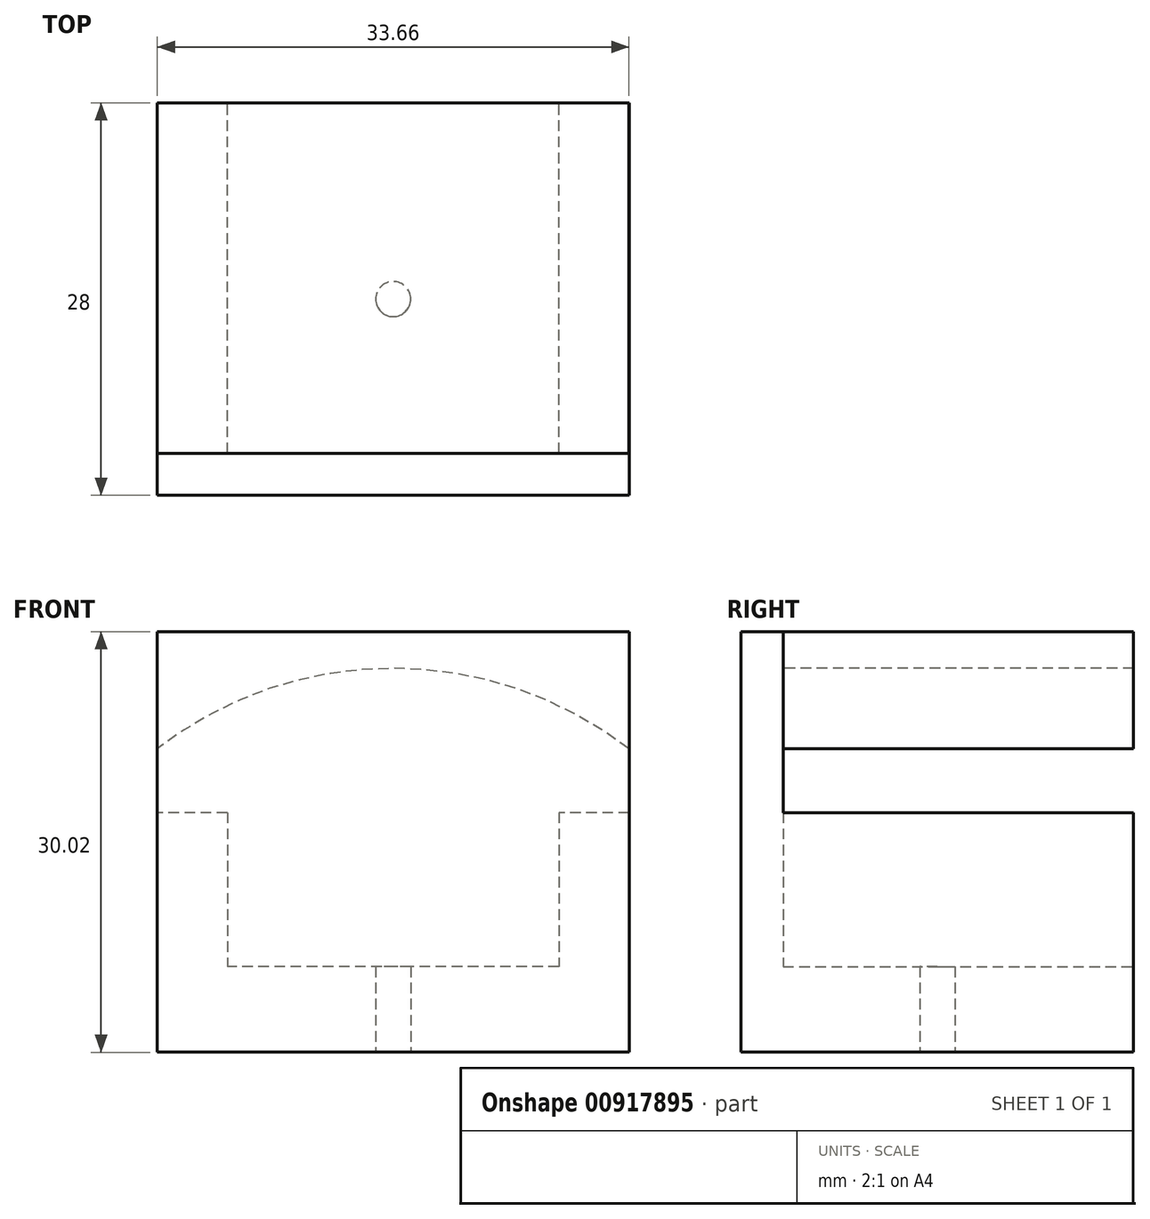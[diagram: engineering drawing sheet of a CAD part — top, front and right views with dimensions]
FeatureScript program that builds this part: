
annotation { "Feature Type Name" : "Feature", "Feature Type Description" : "" }
export const myFeature = defineFeature(function(context is Context, id is Id, definition is map)
    precondition{}
    {
        {
            var Q0;
            Q0=qCreatedBy(makeId("Front.planeOp"),FACE);
            var sketch = newSketch(context, id + "F0", { "sketchPlane" : qUnion([Q0])});
            skLineSegment(sketch, "E0.bottom", {"start": v(-12.4, 16.5) * mm, "end": v(21.24, 16.5) * mm});
            skLineSegment(sketch, "E0.top", {"start": v(-12.4, -13.6) * mm, "end": v(21.24, -13.6) * mm});
            skLineSegment(sketch, "E0.left", {"start": v(-12.4, 16.5) * mm, "end": v(-12.4, -13.6) * mm});
            skLineSegment(sketch, "E0.right", {"start": v(21.24, 16.5) * mm, "end": v(21.24, -13.6) * mm});
            skSolve(sketch);
        }
        {
            var Q0;
            Q0=makeQuery(id+"F0.imprint","IMPRINT",FACE,{"disambiguationData":[TD([[makeQuery(id+"F0.imprint","IMPRINT",EDGE,{"derivedFrom":sQuery(id+"F0.wireOp",EDGE,"E0.bottom")}),-1.0]])]});
            extrude(context, id + "F1", {"entities" : qUnion([Q0]), "depth" : 25 * mm, "offsetDistance" : 25 * mm});
        }
        {
            var Q0;
            Q0=makeQuery(id+"F1.opExtrude","CAP_FACE",FACE,{"disambiguationData":[OSD([sQuery(id+"F0.wireOp",EDGE,"E0.bottom"),sQuery(id+"F0.wireOp",EDGE,"E0.top"),sQuery(id+"F0.wireOp",EDGE,"E0.left"),sQuery(id+"F0.wireOp",EDGE,"E0.right")])],"isStart":false});
            var sketch = newSketch(context, id + "F2", { "sketchPlane" : qUnion([Q0])});
            skLineSegment(sketch, "E1", {"start": v(4.43, -13.6) * mm, "end": v(4.43, 16.5) * mm});
            skSolve(sketch);
        }
        {
            var Q0;
            Q0=sQuery(id+"F2.wireOp",VERTEX,"E1.start");
            var Q1;
            Q1=makeQuery(id+"F1.opExtrude","SWEPT_BODY",BODY,{"disambiguationData":[OSD([sQuery(id+"F0.wireOp",EDGE,"E0.bottom"),sQuery(id+"F0.wireOp",EDGE,"E0.top"),sQuery(id+"F0.wireOp",EDGE,"E0.left"),sQuery(id+"F0.wireOp",EDGE,"E0.right")])]});
            hole(context, id + "F3", {"style" : HoleStyle.SIMPLE, "endStyle" : HoleEndStyle.BLIND, "holeDiameter" : 55 * mm, "majorDiameter" : 5 * mm, "holeDepth" : 50 * mm, "isTappedThrough" : true, "tappedDepth" : 12 * mm, "tapClearance" : 3, "locations" : qUnion([Q0]), "scope" : qUnion([Q1])});
        }
        {
            var Q0;
            Q0=makeQuery(id+"F1.opExtrude","CAP_FACE",FACE,{"disambiguationData":[OSD([sQuery(id+"F0.wireOp",EDGE,"E0.bottom"),sQuery(id+"F0.wireOp",EDGE,"E0.top"),sQuery(id+"F0.wireOp",EDGE,"E0.left"),sQuery(id+"F0.wireOp",EDGE,"E0.right")])],"isStart":false});
            var sketch = newSketch(context, id + "F4", { "sketchPlane" : qUnion([Q0])});
            skLineSegment(sketch, "E2.bottom", {"start": v(-12.4, 16.5) * mm, "end": v(21.27, 16.5) * mm});
            skLineSegment(sketch, "E2.top", {"start": v(-12.4, -13.52) * mm, "end": v(21.27, -13.52) * mm});
            skLineSegment(sketch, "E2.left", {"start": v(-12.4, 16.5) * mm, "end": v(-12.4, -13.52) * mm});
            skLineSegment(sketch, "E2.right", {"start": v(21.27, 16.5) * mm, "end": v(21.27, -13.52) * mm});
            skSolve(sketch);
        }
        {
            var Q0;
            Q0 = qSketchRegion(id + "F4", true);
            extrude(context, id + "F5", {"entities" : qUnion([Q0]), "depth" : 3 * mm, "offsetDistance" : 25 * mm});
        }
        {
            var Q0;
            Q0=makeQuery(id+"F5.opExtrude","CAP_FACE",FACE,{"disambiguationData":[OSD([sQuery(id+"F4.wireOp",EDGE,"E2.bottom"),sQuery(id+"F4.wireOp",EDGE,"E2.top"),sQuery(id+"F4.wireOp",EDGE,"E2.left"),sQuery(id+"F4.wireOp",EDGE,"E2.right")])],"isStart":true});
            var sketch = newSketch(context, id + "F6", { "sketchPlane" : qUnion([Q0])});
            skLineSegment(sketch, "E3.bottom", {"start": v(-21.27, -13.52) * mm, "end": v(12.4, -13.52) * mm});
            skLineSegment(sketch, "E3.top", {"start": v(-21.27, -7.4) * mm, "end": v(12.4, -7.4) * mm});
            skLineSegment(sketch, "E3.left", {"start": v(-21.27, -13.52) * mm, "end": v(-21.27, -7.4) * mm});
            skLineSegment(sketch, "E3.right", {"start": v(12.4, -13.52) * mm, "end": v(12.4, -7.4) * mm});
            skSolve(sketch);
        }
        {
            var Q0;
            Q0=makeQuery(id+"F6.imprint","IMPRINT",FACE,{"disambiguationData":[TD([[makeQuery(id+"F6.imprint","IMPRINT",EDGE,{"derivedFrom":sQuery(id+"F6.wireOp",EDGE,"E3.bottom")}),-1.0]])]});
            extrude(context, id + "F7", {"entities" : qUnion([Q0]), "operationType" : NewBodyOperationType.ADD, "depth" : 25 * mm, "offsetDistance" : 25 * mm});
        }
        {
            var Q0;
            Q0=makeQuery(id+"F7.boolean.opBoolean","MERGE",FACE,{"derivedFrom":[makeQuery(id+"F5.opExtrude","SWEPT_FACE",FACE,{"disambiguationData":[OSD([sQuery(id+"F4.wireOp",EDGE,"E2.top")])]}),makeQuery(id+"F7.opExtrude","SWEPT_FACE",FACE,{"disambiguationData":[OSD([sQuery(id+"F6.wireOp",EDGE,"E3.bottom")])]})]});
            var sketch = newSketch(context, id + "F8", { "sketchPlane" : qUnion([Q0])});
            skLineSegment(sketch, "E4", {"start": v(-12.4, 28) * mm, "end": v(21.27, 0) * mm});
            skLineSegment(sketch, "E5", {"start": v(21.27, 0) * mm, "end": v(21.27, 28) * mm});
            skLineSegment(sketch, "E6", {"start": v(21.27, 28) * mm, "end": v(-12.4, 0) * mm});
            skLineSegment(sketch, "E7", {"start": v(-12.4, 0) * mm, "end": v(4.44, 14) * mm});
            skLineSegment(sketch, "E8", {"start": v(4.44, 14) * mm, "end": v(4.44, 0.89) * mm});
            skLineSegment(sketch, "E9", {"start": v(4.44, 0.89) * mm, "end": v(4.44, 28) * mm});
            skSolve(sketch);
        }
        {
            var Q0;
            Q0=sQuery(id+"F8.wireOp",VERTEX,"E7.end");
            var Q1;
            Q1=makeQuery(id+"F5.opExtrude","SWEPT_BODY",BODY,{"disambiguationData":[OSD([sQuery(id+"F4.wireOp",EDGE,"E2.bottom"),sQuery(id+"F4.wireOp",EDGE,"E2.top"),sQuery(id+"F4.wireOp",EDGE,"E2.left"),sQuery(id+"F4.wireOp",EDGE,"E2.right")])]});
            hole(context, id + "F9", {"style" : HoleStyle.SIMPLE, "endStyle" : HoleEndStyle.BLIND, "holeDiameter" : 2.5 * mm, "majorDiameter" : 5 * mm, "holeDepth" : 10 * mm, "isTappedThrough" : true, "tappedDepth" : 12 * mm, "tapClearance" : 3, "locations" : qUnion([Q0]), "scope" : qUnion([Q1])});
        }
        {
            var Q0;
            Q0=makeQuery(id+"F7.opExtrude","SWEPT_FACE",FACE,{"disambiguationData":[OSD([sQuery(id+"F6.wireOp",EDGE,"E3.top")])]});
            var sketch = newSketch(context, id + "F10", { "sketchPlane" : qUnion([Q0])});
            skLineSegment(sketch, "E10.bottom", {"start": v(-12.4, -25) * mm, "end": v(-7.4, -25) * mm});
            skLineSegment(sketch, "E10.top", {"start": v(-12.4, 0) * mm, "end": v(-7.4, 0) * mm});
            skLineSegment(sketch, "E10.left", {"start": v(-12.4, -25) * mm, "end": v(-12.4, 0) * mm});
            skLineSegment(sketch, "E10.right", {"start": v(-7.4, -25) * mm, "end": v(-7.4, 0) * mm});
            skLineSegment(sketch, "E11.MirrorCS", {"start": v(16.27, -25) * mm, "end": v(16.27, 0) * mm});
            skLineSegment(sketch, "E12.MirrorCS", {"start": v(21.27, -25) * mm, "end": v(21.27, 0) * mm});
            skLineSegment(sketch, "E13.MirrorCS", {"start": v(21.27, 0) * mm, "end": v(16.27, 0) * mm});
            skLineSegment(sketch, "E14.MirrorCS", {"start": v(21.27, -25) * mm, "end": v(16.27, -25) * mm});
            skSolve(sketch);
        }
        {
            var Q0;
            Q0=makeQuery(id+"F10.imprint","IMPRINT",FACE,{"disambiguationData":[TD([[makeQuery(id+"F10.imprint","IMPRINT",EDGE,{"derivedFrom":sQuery(id+"F10.wireOp",EDGE,"E10.bottom")}),-1.0]])]});
            extrude(context, id + "F11", {"entities" : qUnion([Q0]), "operationType" : NewBodyOperationType.ADD, "depth" : 11 * mm, "offsetDistance" : 25 * mm});
        }
        {
            var Q0;
            Q0=makeQuery(id+"F10.imprint","IMPRINT",FACE,{"disambiguationData":[TD([[makeQuery(id+"F10.imprint","IMPRINT",EDGE,{"derivedFrom":sQuery(id+"F10.wireOp",EDGE,"E11.MirrorCS")}),-1.0]])]});
            extrude(context, id + "F12", {"entities" : qUnion([Q0]), "operationType" : NewBodyOperationType.ADD, "depth" : 11 * mm, "offsetDistance" : 25 * mm});
        }
    });
